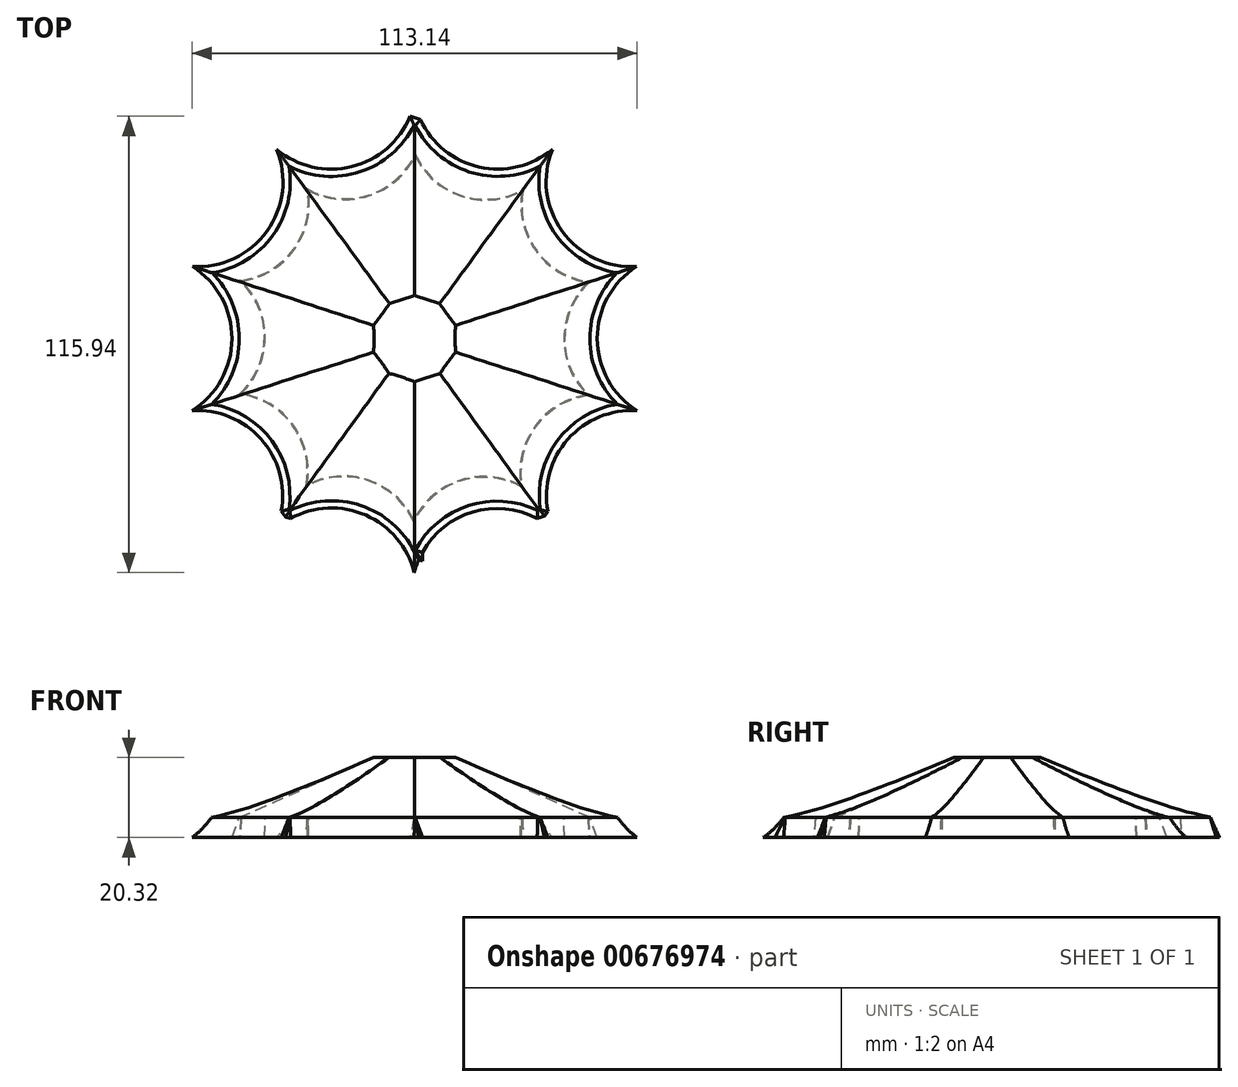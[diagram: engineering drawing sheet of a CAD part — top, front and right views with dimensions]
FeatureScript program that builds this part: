
annotation { "Feature Type Name" : "Feature", "Feature Type Description" : "" }
export const myFeature = defineFeature(function(context is Context, id is Id, definition is map)
    precondition{}
    {
        {
            var Q0;
            Q0=qCreatedBy(makeId("Top.planeOp"),FACE);
            var sketch = newSketch(context, id + "F0", { "sketchPlane" : qUnion([Q0])});
            skArc(sketch, "E0.cCircle", {"start": v(-8, 11) * mm, "mid": v(-8, 10.99) * mm, "end": v(-8.02, 10.98) * mm, "construction": true});
            skLineSegment(sketch, "E0.1", {"start": v(-12.85, -4.32) * mm, "end": v(-12.93, -4.2) * mm});
            skLineSegment(sketch, "E0.7", {"start": v(12.93, 4.2) * mm, "end": v(12.93, 4.06) * mm});
            skLineSegment(sketch, "E0.8", {"start": v(8.01, -10.97) * mm, "end": v(8, -11) * mm});
            skArc(sketch, "E1.cCircle", {"start": v(-51.43, -16.71) * mm, "mid": v(-51.4, -16.8) * mm, "end": v(-51.38, -16.87) * mm, "construction": true});
            skLineSegment(sketch, "E1.0", {"start": v(31.9, -43.67) * mm, "end": v(31.3, -43.86) * mm});
            skLineSegment(sketch, "E1.1", {"start": v(0.14, -54.07) * mm, "end": v(-0.25, -53.95) * mm});
            skLineSegment(sketch, "E1.2", {"start": v(-31.67, -43.83) * mm, "end": v(-31.91, -43.5) * mm});
            skLineSegment(sketch, "E1.3", {"start": v(-51.39, -16.84) * mm, "end": v(-51.39, -16.67) * mm});
            skLineSegment(sketch, "E1.6", {"start": v(-0.14, 54.07) * mm, "end": v(0.19, 53.97) * mm});
            skLineSegment(sketch, "E1.7", {"start": v(31.67, 43.83) * mm, "end": v(31.88, 43.55) * mm});
            skLineSegment(sketch, "E1.8", {"start": v(51.39, 16.84) * mm, "end": v(51.39, 16.5) * mm});
            skLineSegment(sketch, "E1.9", {"start": v(51.47, -16.58) * mm, "end": v(51.25, -16.89) * mm});
            skArc(sketch, "E2", {"start": v(-51.47, 16.58) * mm, "mid": v(-36.03, 26.04) * mm, "end": v(-31.9, 43.67) * mm});
            skArc(sketch, "E3.MirrorCS", {"start": v(51.47, 16.58) * mm, "mid": v(36.03, 26.04) * mm, "end": v(31.9, 43.67) * mm});
            skLineSegment(sketch, "E4", {"start": v(-8.02, 10.98) * mm, "end": v(-8.01, 10.97) * mm});
            skArc(sketch, "E5.MirrorCS", {"start": v(-0.14, 54.07) * mm, "mid": v(-13.84, 42.24) * mm, "end": v(-31.9, 43.67) * mm});
            skArc(sketch, "E6.MirrorCS", {"start": v(0.14, 54.07) * mm, "mid": v(13.84, 42.24) * mm, "end": v(31.9, 43.67) * mm});
            skLineSegment(sketch, "E7", {"start": v(-12.89, -4.33) * mm, "end": v(-12.85, -4.32) * mm});
            skArc(sketch, "E8.MirrorCS", {"start": v(51.47, 16.58) * mm, "mid": v(44.54, -0.15) * mm, "end": v(51.55, -16.84) * mm});
            skArc(sketch, "E9.MirrorCS", {"start": v(31.98, -43.93) * mm, "mid": v(36.11, -26.3) * mm, "end": v(51.55, -16.84) * mm});
            skArc(sketch, "E10.MirrorCS", {"start": v(31.76, -44.09) * mm, "mid": v(13.71, -42.57) * mm, "end": v(-0.05, -54.33) * mm});
            skArc(sketch, "E11.MirrorCS", {"start": v(-31.81, -43.93) * mm, "mid": v(-13.76, -42.5) * mm, "end": v(-0.05, -54.33) * mm});
            skArc(sketch, "E12.MirrorCS", {"start": v(-31.98, -43.93) * mm, "mid": v(-36.11, -26.3) * mm, "end": v(-51.55, -16.84) * mm});
            skArc(sketch, "E13.MirrorCS", {"start": v(-51.47, 16.58) * mm, "mid": v(-44.54, -0.15) * mm, "end": v(-51.55, -16.84) * mm});
            skArc(sketch, "E14.trimOffspring", {"start": v(0.14, 54.07) * mm, "mid": v(0, 54.07) * mm, "end": v(-0.14, 54.07) * mm, "construction": true});
            skArc(sketch, "E15.trimOffspring", {"start": v(31.9, 43.67) * mm, "mid": v(31.78, 43.75) * mm, "end": v(31.67, 43.83) * mm, "construction": true});
            skArc(sketch, "E16.trimOffspring", {"start": v(51.47, 16.58) * mm, "mid": v(51.43, 16.7) * mm, "end": v(51.39, 16.84) * mm, "construction": true});
            skArc(sketch, "E17.trimOffspring", {"start": v(51.38, -16.87) * mm, "mid": v(51.42, -16.72) * mm, "end": v(51.47, -16.58) * mm, "construction": true});
            skLineSegment(sketch, "E18.trimOffspring", {"start": v(31.93, -43.62) * mm, "end": v(31.9, -43.67) * mm});
            skArc(sketch, "E19.trimOffspring", {"start": v(31.5, -43.95) * mm, "mid": v(31.72, -43.8) * mm, "end": v(31.93, -43.64) * mm, "construction": true});
            skLineSegment(sketch, "E20.trimOffspring", {"start": v(-31.64, -43.84) * mm, "end": v(-31.67, -43.83) * mm});
            skArc(sketch, "E21.trimOffspring", {"start": v(-0.18, -54.07) * mm, "mid": v(-0.02, -54.07) * mm, "end": v(0.14, -54.07) * mm, "construction": true});
            skArc(sketch, "E22.trimOffspring", {"start": v(-31.93, -43.64) * mm, "mid": v(-31.8, -43.74) * mm, "end": v(-31.65, -43.84) * mm, "construction": true});
            skLineSegment(sketch, "E23.trimOffspring", {"start": v(-51.36, -16.87) * mm, "end": v(-51.39, -16.84) * mm});
            skLineSegment(sketch, "E24.trimOffspring", {"start": v(8.01, -10.97) * mm, "end": v(8.02, -10.98) * mm});
            skLineSegment(sketch, "E25.trimOffspring", {"start": v(12.93, 4.06) * mm, "end": v(12.97, 4.07) * mm});
            skLineSegment(sketch, "E26.trimOffspring", {"start": v(0, 0) * mm, "end": v(0.08, -0.12) * mm});
            skLineSegment(sketch, "E27", {"start": v(31.9, 43.67) * mm, "end": v(31.84, 43.6) * mm});
            skLineSegment(sketch, "E28", {"start": v(0.14, -53.97) * mm, "end": v(0.14, -54.07) * mm});
            skArc(sketch, "E29.trimOffspring", {"start": v(12.97, 4.07) * mm, "mid": v(12.95, 4.14) * mm, "end": v(12.93, 4.2) * mm, "construction": true});
            skArc(sketch, "E30.trimOffspring", {"start": v(8, -11) * mm, "mid": v(8, -10.99) * mm, "end": v(8.02, -10.98) * mm, "construction": true});
            skArc(sketch, "E31.trimOffspring", {"start": v(-12.93, -4.2) * mm, "mid": v(-12.9, -4.27) * mm, "end": v(-12.89, -4.33) * mm, "construction": true});
            skLineSegment(sketch, "E32.trimOffspring", {"start": v(51.39, 16.55) * mm, "end": v(51.47, 16.58) * mm});
            skPoint(sketch, "E33.orphan", {"position": v(-12.93, 4.2) * mm});
            skPoint(sketch, "E34.orphan", {"position": v(12.93, -4.2) * mm});
            skPoint(sketch, "E0.0.start.orphan", {"position": v(0, -13.6) * mm});
            skPoint(sketch, "E35.orphan", {"position": v(-8, -11) * mm});
            skSolve(sketch);
        }
        {
            var Q0;
            Q0 = qSketchRegion(id + "F0", true);
            extrude(context, id + "F1", {"entities" : qUnion([Q0]), "depth" : 15.24 * mm, "offsetDistance" : 25.4 * mm, "hasDraft" : true, "draftAngle" : 66 * degree, "draftPullDirection" : true, "hasSecondDirection" : true, "secondDirectionOppositeDirection" : true, "secondDirectionDepth" : 5.08 * mm, "hasSecondDirectionDraft" : true, "secondDirectionDraftAngle" : 20 * degree});
        }
        {
            var Q0;
            Q0=makeQuery(id+"F1.opExtrude","CAP_FACE",FACE,{"disambiguationData":[OSD([sQuery(id+"F0.wireOp",EDGE,"E1.0"),sQuery(id+"F0.wireOp",EDGE,"E1.1"),sQuery(id+"F0.wireOp",EDGE,"E1.2"),sQuery(id+"F0.wireOp",EDGE,"E1.6"),sQuery(id+"F0.wireOp",EDGE,"E2"),sQuery(id+"F0.wireOp",EDGE,"E3.MirrorCS"),sQuery(id+"F0.wireOp",EDGE,"E5.MirrorCS"),sQuery(id+"F0.wireOp",EDGE,"E6.MirrorCS"),sQuery(id+"F0.wireOp",EDGE,"E8.MirrorCS"),sQuery(id+"F0.wireOp",EDGE,"E9.MirrorCS"),sQuery(id+"F0.wireOp",EDGE,"E10.MirrorCS"),sQuery(id+"F0.wireOp",EDGE,"E11.MirrorCS"),sQuery(id+"F0.wireOp",EDGE,"E12.MirrorCS"),sQuery(id+"F0.wireOp",EDGE,"E13.MirrorCS"),sQuery(id+"F0.wireOp",EDGE,"E18.trimOffspring"),sQuery(id+"F0.wireOp",EDGE,"E20.trimOffspring"),sQuery(id+"F0.wireOp",EDGE,"E28")])],"isStart":true});
            var sketch = newSketch(context, id + "F2", { "sketchPlane" : qUnion([Q0])});
            skPoint(sketch, "E36.0.midPoint", {"position": v(16.4, -43.46) * mm});
            skArc(sketch, "E37", {"start": v(-27.62, 37.7) * mm, "mid": v(-11.92, 36.22) * mm, "end": v(-0.18, 46.74) * mm});
            skArc(sketch, "E38.MirrorCS", {"start": v(27.33, 37.92) * mm, "mid": v(11.65, 36.31) * mm, "end": v(-0.18, 46.74) * mm});
            skArc(sketch, "E39.MirrorCS", {"start": v(44.51, -14.27) * mm, "mid": v(30.94, -22.3) * mm, "end": v(27.62, -37.7) * mm});
            skArc(sketch, "E40.MirrorCS", {"start": v(0.18, -46.74) * mm, "mid": v(11.92, -36.22) * mm, "end": v(27.62, -37.7) * mm});
            skArc(sketch, "E41.MirrorCS", {"start": v(-44.4, -14.61) * mm, "mid": v(-30.77, -22.53) * mm, "end": v(-27.33, -37.92) * mm});
            skArc(sketch, "E42.MirrorCS", {"start": v(0.18, -46.74) * mm, "mid": v(-11.65, -36.31) * mm, "end": v(-27.33, -37.92) * mm});
            skArc(sketch, "E43.MirrorCS", {"start": v(-44.4, -14.61) * mm, "mid": v(-38.14, -0.15) * mm, "end": v(-44.51, 14.27) * mm});
            skArc(sketch, "E44.MirrorCS", {"start": v(-27.62, 37.7) * mm, "mid": v(-30.94, 22.3) * mm, "end": v(-44.51, 14.27) * mm});
            skArc(sketch, "E45.MirrorCS", {"start": v(27.33, 37.92) * mm, "mid": v(30.77, 22.53) * mm, "end": v(44.4, 14.61) * mm});
            skArc(sketch, "E46.MirrorCS", {"start": v(44.51, -14.27) * mm, "mid": v(38.14, 0.15) * mm, "end": v(44.4, 14.61) * mm});
            skPoint(sketch, "E47.orphan", {"position": v(30.11, -38.94) * mm});
            skPoint(sketch, "E36.1.start.orphan", {"position": v(2.67, -47.97) * mm});
            skSolve(sketch);
        }
        {
            var Q0;
            Q0 = qSketchRegion(id + "F2", true);
            extrude(context, id + "F3", {"entities" : qUnion([Q0]), "oppositeDirection" : true, "depth" : 5.08 * mm, "offsetDistance" : 25.4 * mm, "hasDraft" : true, "draftAngle" : 2 * degree, "draftPullDirection" : true});
        }
    });
